# Revit family: 13.Бактерицидная секция для прямоугольных каналов SBOW
name_source: partatom
category: Оборудование
revit_build: Autodesk Revit 2016 (Build: 20151209_0715(x64)
units: mm (PartAtom-declared; Revit-internal decimal feet)

## family parameters
Всегда вертикально = Да
На основе рабочей плоскости = Нет
Общий = Нет
При загрузке вырезать с полостями = Нет
Размер круглого соединителя = Использовать диаметр
Тип детали = Нормальный
Точка расчета площади = Нет

## types (36) — shared parameters
Глубина среза = 15 мм
Единица измерения = шт.
Завод изготовитель = KORF
И = 1440 мм
Ключевая пометка = Вентиляция
Материал = Сталь серая
Наименование и тех.хар-ка = Бактерицидная секция для прямоугольных каналов
Отступ = 20 мм
Раздел = ОВ

## per-type parameters (varying)
| type | А | Б | Высота | Г | Д | Д1 | Е | Ж | З | Масса единицы | Мощность, кВт | Размер В | Тип, марка, обозначение | Ширина |
| 40-20/143 | 400 мм | 200 мм | 200 мм | 220 мм | 440 мм | 110 мм | 280 мм | 9 мм | 235 мм | 42 кг | 1 Вт | 420 мм | SBOW 40-20/143 | 400 мм |
| 40-20/95 | 400 мм | 200 мм | 200 мм | 220 мм | 440 мм | 110 мм | 280 мм | 9 мм | 235 мм | 33,5 кг | 0 Вт | 420 мм | SBOW 40-20/95 | 400 мм |
| 40-20/63 | 400 мм | 200 мм | 200 мм | 220 мм | 440 мм | 110 мм | 280 мм | 9 мм | 235 мм | 27,4 кг | 0 Вт | 420 мм | SBOW 40-20/63 | 400 мм |
| 40-20/32 | 400 мм | 200 мм | 200 мм | 220 мм | 440 мм | 110 мм | 280 мм | 9 мм | 235 мм | 21.3 кг | 0 Вт | 420 мм | SBOW 40-20/63 | 400 мм |
| 50-25/159 | 500 мм | 250 мм | 250 мм | 270 мм | 540 мм | 135 мм | 330 мм | 9 мм | 285 мм | 48.5 кг | 1 Вт | 520 мм | SBOW 50-25/159 | 500 мм |
| 50-25/111 | 500 мм | 250 мм | 250 мм | 270 мм | 540 мм | 135 мм | 330 мм | 9 мм | 285 мм | 40.5 кг | 1 Вт | 520 мм | SBOW 50-25/111 | 500 мм |
| 50-25/63 | 500 мм | 250 мм | 250 мм | 270 мм | 540 мм | 135 мм | 330 мм | 9 мм | 285 мм | 31.5 кг | 0 Вт | 520 мм | SBOW 50-25/63 | 500 мм |
| 50-25/32 | 500 мм | 250 мм | 250 мм | 270 мм | 540 мм | 135 мм | 330 мм | 9 мм | 285 мм | 25.4 кг | 0 Вт | 520 мм | SBOW 50-25/32 | 500 мм |
| 50-30/174 | 500 мм | 300 мм | 300 мм | 320 мм | 540 мм | 135 мм | 380 мм | 9 мм | 335 мм | 51.5 кг | 1 Вт | 520 мм | SBOW 50-30/174 | 500 мм |
| 50-30/111 | 500 мм | 300 мм | 300 мм | 320 мм | 540 мм | 135 мм | 380 мм | 9 мм | 335 мм | 41.5 кг | 1 Вт | 520 мм | SBOW 50-30/111 | 500 мм |
| 50-30/79 | 500 мм | 300 мм | 300 мм | 320 мм | 540 мм | 135 мм | 380 мм | 9 мм | 335 мм | 36.2 кг | 0 Вт | 520 мм | SBOW 50-30/79 | 500 мм |
| 50-30/47 | 500 мм | 300 мм | 300 мм | 320 мм | 540 мм | 135 мм | 380 мм | 9 мм | 335 мм | 30.1 кг | 0 Вт | 520 мм | SBOW 50-30/47 | 500 мм |
| 60-30/190 | 600 мм | 300 мм | 300 мм | 320 мм | 640 мм | 160 мм | 380 мм | 9 мм | 335 мм | 57.7 кг | 1 Вт | 620 мм | SBOW 60-30/190 | 600 мм |
| 60-30/127 | 600 мм | 300 мм | 300 мм | 320 мм | 640 мм | 160 мм | 380 мм | 9 мм | 335 мм | 47 кг | 1 Вт | 620 мм | SBOW 60-30/127 | 600 мм |
| 60-30/79 | 600 мм | 300 мм | 300 мм | 320 мм | 640 мм | 160 мм | 380 мм | 9 мм | 335 мм | 38.8 кг | 0 Вт | 620 мм | SBOW 60-30/79 | 600 мм |
| 60-30/47 | 600 мм | 300 мм | 300 мм | 320 мм | 640 мм | 160 мм | 380 мм | 9 мм | 335 мм | 32.7 кг | 0 Вт | 620 мм | SBOW 60-30/47 | 600 мм |
| 60-35/222 | 600 мм | 350 мм | 350 мм | 370 мм | 640 мм | 160 мм | 430 мм | 9 мм | 385 мм | 65 кг | 1 Вт | 620 мм | SBOW 60-35/222 | 600 мм |
| 60-35/143 | 600 мм | 350 мм | 350 мм | 370 мм | 640 мм | 160 мм | 430 мм | 9 мм | 385 мм | 53.4 кг | 1 Вт | 620 мм | SBOW 60-35/143 | 600 мм |
| 60-35/95 | 600 мм | 350 мм | 350 мм | 370 мм | 640 мм | 160 мм | 430 мм | 9 мм | 385 мм | 45.3 кг | 0 Вт | 620 мм | SBOW 60-35/95 | 600 мм |
| 60-35/63 | 600 мм | 350 мм | 350 мм | 370 мм | 640 мм | 160 мм | 430 мм | 9 мм | 385 мм | 39.2 кг | 0 Вт | 620 мм | SBOW 60-35/63 | 600 мм |
| 70-40/270 | 700 мм | 400 мм | 400 мм | 420 мм | 740 мм | 185 мм | 480 мм | 9 мм | 435 мм | 91.5 кг | 1 Вт | 720 мм | SBOW 70-40/270 | 700 мм |
| 70-40/174 | 700 мм | 400 мм | 400 мм | 420 мм | 740 мм | 185 мм | 480 мм | 9 мм | 435 мм | 75,3 кг | 1 Вт | 720 мм | SBOW 70-40/174 | 700 мм |
| 70-40/111 | 700 мм | 400 мм | 400 мм | 420 мм | 740 мм | 185 мм | 480 мм | 9 мм | 435 мм | 64.5 кг | 1 Вт | 720 мм | SBOW 70-40/111 | 700 мм |
| 70-40/63 | 700 мм | 400 мм | 400 мм | 420 мм | 740 мм | 185 мм | 480 мм | 9 мм | 435 мм | 55.4 кг | 0 Вт | 720 мм | SBOW 70-40/111 | 700 мм |
| 80-50/302 | 800 мм | 500 мм | 500 мм | 520 мм | 840 мм | 210 мм | 580 мм | 9 мм | 535 мм | 103.5 кг | 1 Вт | 820 мм | SBOW 80-50/302 | 800 мм |
| 80-50/206 | 800 мм | 500 мм | 500 мм | 520 мм | 840 мм | 210 мм | 580 мм | 9 мм | 535 мм | 88 кг | 1 Вт | 820 мм | SBOW 80-50/206 | 800 мм |
| 80-50/127 | 800 мм | 500 мм | 500 мм | 520 мм | 840 мм | 210 мм | 580 мм | 9 мм | 535 мм | 74 кг | 1 Вт | 820 мм | SBOW 80-50/127 | 800 мм |
| 80-50/79 | 800 мм | 500 мм | 500 мм | 520 мм | 840 мм | 210 мм | 580 мм | 9 мм | 535 мм | 64.9 кг | 0 Вт | 820 мм | SBOW 80-50/79 | 800 мм |
| 90-50/365 | 900 мм | 500 мм | 500 мм | 530 мм | 960 мм | 240 мм | 580 мм | 11 мм | 535 мм | 118.5 кг | 2 Вт | 930 мм | SBOW 90-50/365 | 900 мм |
| 90-50/238 | 900 мм | 500 мм | 500 мм | 530 мм | 960 мм | 240 мм | 580 мм | 11 мм | 535 мм | 97 кг | 1 Вт | 930 мм | SBOW 90-50/238 | 900 мм |
| 90-50/159 | 900 мм | 500 мм | 500 мм | 530 мм | 960 мм | 240 мм | 580 мм | 11 мм | 535 мм | 83.2 кг | 1 Вт | 930 мм | SBOW 90-50/159 | 900 мм |
| 90-50/95 | 900 мм | 500 мм | 500 мм | 530 мм | 960 мм | 240 мм | 580 мм | 11 мм | 535 мм | 71 кг | 0 Вт | 930 мм | SBOW 90-50/95 | 900 мм |
| 100-50/397 | 1000 мм | 500 мм | 500 мм | 530 мм | 1060 мм | 265 мм | 580 мм | 11 мм | 535 мм | 127.3 кг | 2 Вт | 1030 мм | SBOW 100-50/397 | 1000 мм |
| 100-50/270 | 1000 мм | 500 мм | 500 мм | 530 мм | 1060 мм | 265 мм | 580 мм | 11 мм | 535 мм | 105.7 кг | 1 Вт | 1030 мм | SBOW 100-50/270 | 1000 мм |
| 100-50/190 | 1000 мм | 500 мм | 500 мм | 530 мм | 1060 мм | 265 мм | 580 мм | 11 мм | 535 мм | 92.2 кг | 1 Вт | 1030 мм | SBOW 100-50/190 | 1000 мм |
| 100-50/111 | 1000 мм | 500 мм | 500 мм | 530 мм | 1060 мм | 265 мм | 580 мм | 11 мм | 535 мм | 77 кг | 1 Вт | 1030 мм | SBOW 100-50/190 | 1000 мм |
